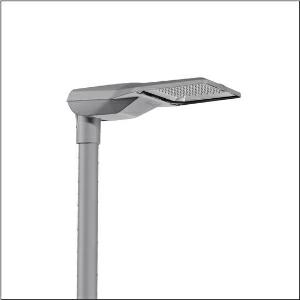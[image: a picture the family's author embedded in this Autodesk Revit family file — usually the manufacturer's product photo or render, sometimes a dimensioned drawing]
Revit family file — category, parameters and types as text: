
# Revit family: streetlight_sl_21_midi___st0_5a_5xe7b43a08lb_42bf
name_source: partatom
category: Lighting Fixtures
units: mm (PartAtom-declared; Revit-internal decimal feet)

## family parameters
Cut with Voids When Loaded = No
Host = Face
Light Source = No
Part Type = Normal
Room Calculation Point = No
Round Connector Dimension = Use Diameter
Shared = No

## types (1)
- --- (1 x LED, 14950 lm, 98.3 W, 4000K)
    Apparent Load = 98 VA
    CIE Flux Codes = 41 75 97 100 100
    Color Rendering = 70
    Color Temperature = 4000K
    Default Elevation = 1800 mm
    Description = Streetlight SL 21 midi, mast luminaire, primary light control with lens, of PMMA, primary optical cover: cover, of toughened safety glass, transparent, light distribution: ST0.5a, light emission: direct distribution, primary light characteristic: asymmetric, installation type: post-top, side-entry, LED, 3G 1.5mm², High Power LED, rated luminous flux: 14.950lm, luminous efficacy: 152lm/W, light colour: 740, colour temperature: 4000K, control: overheat protection, constant luminous flux control, time-dependent luminous flux control, flexible luminous flux parameterisation, mains connection: 220..240V, AC, 50/60Hz, connection cable pre-assembled, cable length: 10,5m, wiring characteristics: H07RN-F, start of lifetime: 98W, end of service life: 101W, reduction: 45W, luminaire housing, of diecast aluminium, powder-coated, Siteco® metallic grey (DB 702S), corrosivity category C5 mid according to DIN EN ISO 12944, please order mast flange separately, inclination adjustable: 0°, 5°, 10°, 15°, sealing non-destructively replaceable, multi-level sealing system, length: 644mm, width: 335mm, height: 110mm, mast flange for spigot size: 42mm (side-entry): 5XC10008XM4, 60/48mm (side-entry/post-top): 5XC10108XM2, 76/60mm (side-entry/post-top): 5XC10108XM1, protection rating (complete): IP66, insulation class (complete): insulation class II (safety insulation), certification: CE, ENEC, ENEC+, VDE, impact resistance: IK09, permissible operating ambient temperature for outdoor applications: -40..+50°C, standard-compliant lighting for roads and squares, packaging unit: 1 piece

Light Distribution: ST0.5a
    Height = 111 mm
    Lamp = 1 x LED
    Lamp Light Flux = 14950 lm
    Lamp Power = 98.3 W
    Lamp count = 1
    Length = 644 mm
    Luminous efficacy = 152 lm/W
    Manufacturer = Siteco
    ModVariant = No
    Model = 5XE7B43A08LB
    Number of Poles = 1
    OnlyDefault = Yes
    Power Factor = 1
    Product Name = Streetlight SL 21 midi | ST0.5a
    Product group = mast luminaire | pylon top
    ProductGroupID = 6100
    Protection Class = Protection class II
    Protection Degree = IP 66
    RLX_Detail_Level = 1
    RLX_Emergency_Light_Flux = 0 lm
    RLX_Emergency_Type = 0
    RLX_Emergency_Type_DB = No
    RlxData = <blob elided: 101817 chars, md5=87952e72>
    Socket = socket
    Standby Power = 0 W
    System Light Flux = 14950 lm
    System Power = 98 W
    Type Comments = factory setting: luminous flux: 100 % | Output Level: 100 % | 1020 mA
    Type Image = l_1004298.jpg
    URL = http://relux.com
    VarID = @adj_144003
    Voltage = 0 V
    Weight = 0.00 kg
    Width = 336 mm

## geometry (parser evidence)
native form markers: Blend x4, Sweep x11
no freeform markers — native parametric forms only
